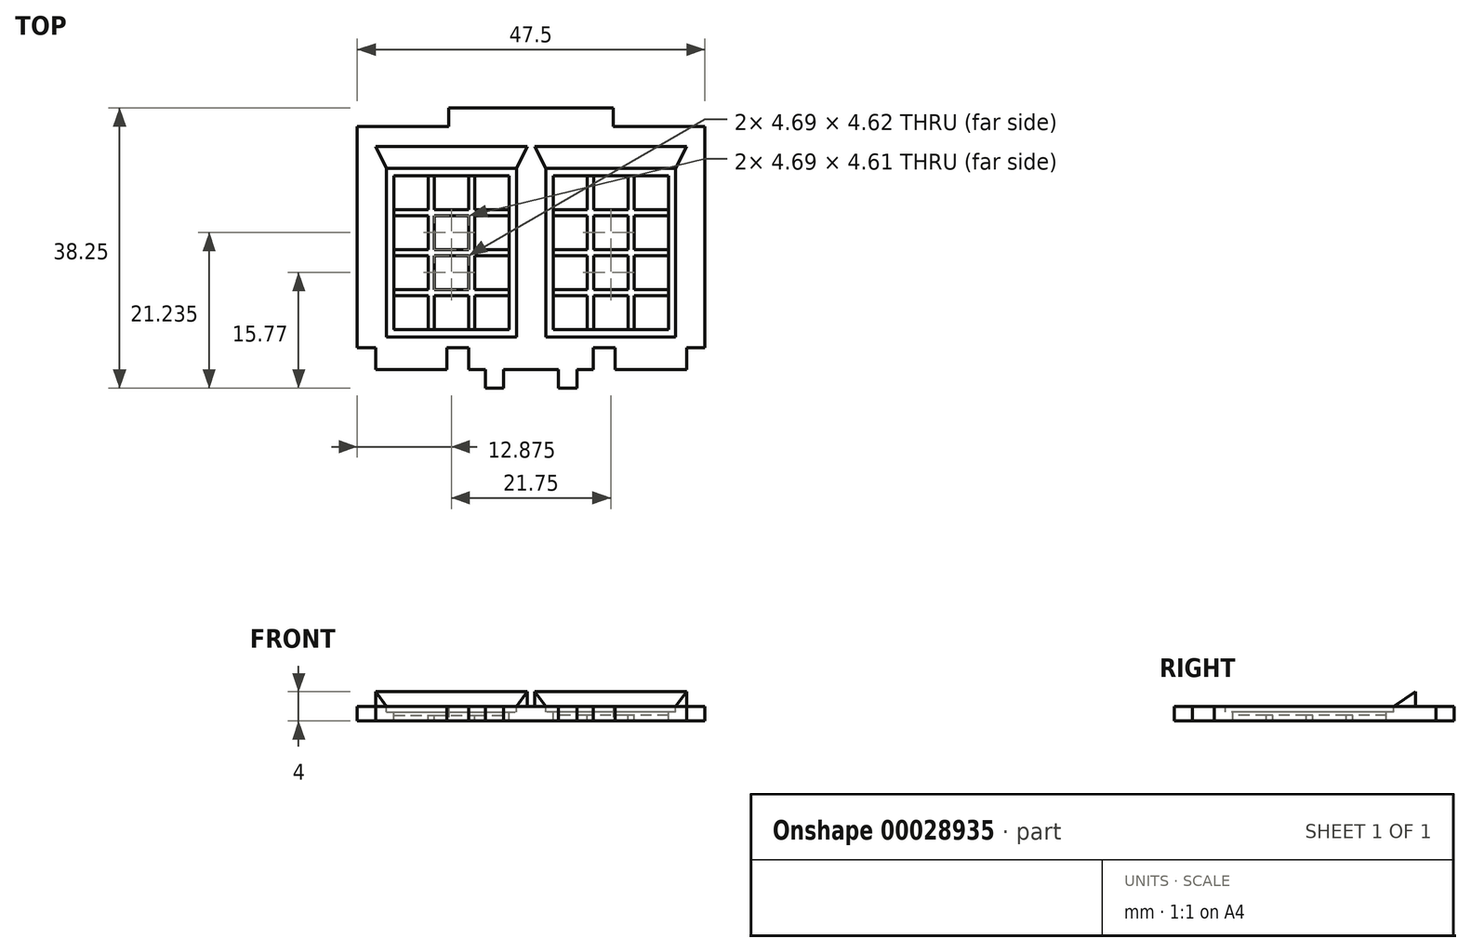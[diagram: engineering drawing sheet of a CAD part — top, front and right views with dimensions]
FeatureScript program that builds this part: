
annotation { "Feature Type Name" : "Feature", "Feature Type Description" : "" }
export const myFeature = defineFeature(function(context is Context, id is Id, definition is map)
    precondition{}
    {
        {
            var Q0;
            Q0=qCreatedBy(makeId("Top.planeOp"),FACE);
            var sketch = newSketch(context, id + "F0", { "sketchPlane" : qUnion([Q0])});
            skLineSegment(sketch, "E0.bottom", {"start": v(-8.5, -5.78) * mm, "end": v(-11.5, -5.78) * mm});
            skLineSegment(sketch, "E0.top", {"start": v(-11.25, 24.47) * mm, "end": v(-23.75, 24.47) * mm});
            skLineSegment(sketch, "E0.right", {"start": v(-23.75, -5.78) * mm, "end": v(-23.75, 24.47) * mm});
            skLineSegment(sketch, "E1.top", {"start": v(-11.25, 26.97) * mm, "end": v(0, 26.97) * mm});
            skLineSegment(sketch, "E1.left", {"start": v(-11.25, 24.47) * mm, "end": v(-11.25, 26.97) * mm});
            skLineSegment(sketch, "E1.right", {"start": v(0, -8.78) * mm, "end": v(0, 26.97) * mm});
            skLineSegment(sketch, "E2.top", {"start": v(-21.25, -8.78) * mm, "end": v(-11.5, -8.78) * mm});
            skLineSegment(sketch, "E2.left", {"start": v(-21.25, -5.78) * mm, "end": v(-21.25, -8.78) * mm});
            skLineSegment(sketch, "E2.right", {"start": v(-11.5, -5.78) * mm, "end": v(-11.5, -8.78) * mm});
            skLineSegment(sketch, "E3.top", {"start": v(-8.5, -8.78) * mm, "end": v(-6.25, -8.78) * mm});
            skLineSegment(sketch, "E3.left", {"start": v(-8.5, -5.78) * mm, "end": v(-8.5, -8.78) * mm});
            skLineSegment(sketch, "E4.top", {"start": v(-6.25, -11.28) * mm, "end": v(-3.75, -11.28) * mm});
            skLineSegment(sketch, "E4.left", {"start": v(-6.25, -8.78) * mm, "end": v(-6.25, -11.28) * mm});
            skLineSegment(sketch, "E4.right", {"start": v(-3.75, -8.78) * mm, "end": v(-3.75, -11.28) * mm});
            skLineSegment(sketch, "E5.trimOffspring", {"start": v(-3.75, -8.78) * mm, "end": v(0, -8.78) * mm});
            skLineSegment(sketch, "E6.trimOffspring", {"start": v(-21.25, -5.78) * mm, "end": v(-23.75, -5.78) * mm});
            skLineSegment(sketch, "E7.MirrorCS", {"start": v(11.25, 26.97) * mm, "end": v(0, 26.97) * mm});
            skLineSegment(sketch, "E8.MirrorCS", {"start": v(11.25, 24.47) * mm, "end": v(11.25, 26.97) * mm});
            skLineSegment(sketch, "E9.MirrorCS", {"start": v(11.25, 24.47) * mm, "end": v(23.75, 24.47) * mm});
            skLineSegment(sketch, "E10.MirrorCS", {"start": v(23.75, -5.78) * mm, "end": v(23.75, 24.47) * mm});
            skLineSegment(sketch, "E11.MirrorCS", {"start": v(21.25, -5.78) * mm, "end": v(23.75, -5.78) * mm});
            skLineSegment(sketch, "E12.MirrorCS", {"start": v(21.25, -5.78) * mm, "end": v(21.25, -8.78) * mm});
            skLineSegment(sketch, "E13.MirrorCS", {"start": v(21.25, -8.78) * mm, "end": v(11.5, -8.78) * mm});
            skLineSegment(sketch, "E14.MirrorCS", {"start": v(11.5, -5.78) * mm, "end": v(11.5, -8.78) * mm});
            skLineSegment(sketch, "E15.MirrorCS", {"start": v(8.5, -5.78) * mm, "end": v(11.5, -5.78) * mm});
            skLineSegment(sketch, "E16.MirrorCS", {"start": v(8.5, -5.78) * mm, "end": v(8.5, -8.78) * mm});
            skLineSegment(sketch, "E17.MirrorCS", {"start": v(8.5, -8.78) * mm, "end": v(6.25, -8.78) * mm});
            skLineSegment(sketch, "E18.MirrorCS", {"start": v(6.25, -8.78) * mm, "end": v(6.25, -11.28) * mm});
            skLineSegment(sketch, "E19.MirrorCS", {"start": v(6.25, -11.28) * mm, "end": v(3.75, -11.28) * mm});
            skLineSegment(sketch, "E20.MirrorCS", {"start": v(3.75, -8.78) * mm, "end": v(3.75, -11.28) * mm});
            skLineSegment(sketch, "E21.MirrorCS", {"start": v(3.75, -8.78) * mm, "end": v(0, -8.78) * mm});
            skSolve(sketch);
        }
        {
            var Q0;
            Q0=makeQuery(id+"F0.imprint","IMPRINT",FACE,{"disambiguationData":[TD([[makeQuery(id+"F0.imprint","IMPRINT",EDGE,{"derivedFrom":sQuery(id+"F0.wireOp",EDGE,"E0.bottom")}),-1.0]])]});
            extrude(context, id + "F1", {"entities" : qUnion([Q0]), "depth" : 2 * mm});
        }
        {
            var Q0;
            Q0=makeQuery(id+"F1.opExtrude","CAP_FACE",FACE,{"disambiguationData":[OSD([sQuery(id+"F0.wireOp",EDGE,"E0.bottom"),sQuery(id+"F0.wireOp",EDGE,"E0.top"),sQuery(id+"F0.wireOp",EDGE,"E0.right"),sQuery(id+"F0.wireOp",EDGE,"E1.top"),sQuery(id+"F0.wireOp",EDGE,"E1.left"),sQuery(id+"F0.wireOp",EDGE,"E1.right"),sQuery(id+"F0.wireOp",EDGE,"E2.top"),sQuery(id+"F0.wireOp",EDGE,"E2.left"),sQuery(id+"F0.wireOp",EDGE,"E2.right"),sQuery(id+"F0.wireOp",EDGE,"E3.top"),sQuery(id+"F0.wireOp",EDGE,"E3.left"),sQuery(id+"F0.wireOp",EDGE,"E4.top"),sQuery(id+"F0.wireOp",EDGE,"E4.left"),sQuery(id+"F0.wireOp",EDGE,"E4.right"),sQuery(id+"F0.wireOp",EDGE,"E5.trimOffspring"),sQuery(id+"F0.wireOp",EDGE,"E6.trimOffspring")])],"isStart":false});
            var sketch = newSketch(context, id + "F2", { "sketchPlane" : qUnion([Q0])});
            skLineSegment(sketch, "E22.bottom", {"start": v(-19.75, 18.72) * mm, "end": v(-2, 18.72) * mm});
            skLineSegment(sketch, "E22.top", {"start": v(-19.75, -4.28) * mm, "end": v(-2, -4.28) * mm});
            skLineSegment(sketch, "E22.left", {"start": v(-19.75, 18.72) * mm, "end": v(-19.75, -4.28) * mm});
            skLineSegment(sketch, "E22.right", {"start": v(-2, 18.72) * mm, "end": v(-2, -4.28) * mm});
            skLineSegment(sketch, "E23", {"start": v(-2, 18.72) * mm, "end": v(-0.5, 21.72) * mm});
            skLineSegment(sketch, "E24", {"start": v(-0.5, 21.72) * mm, "end": v(-21.25, 21.72) * mm});
            skLineSegment(sketch, "E25", {"start": v(-21.25, 21.72) * mm, "end": v(-19.75, 18.72) * mm});
            skLineSegment(sketch, "E26.0", {"start": v(-18.75, 17.72) * mm, "end": v(-3, 17.72) * mm});
            skLineSegment(sketch, "E26.1", {"start": v(-18.75, 17.72) * mm, "end": v(-18.75, -3.28) * mm});
            skLineSegment(sketch, "E26.2", {"start": v(-18.75, -3.28) * mm, "end": v(-3, -3.28) * mm});
            skLineSegment(sketch, "E26.3", {"start": v(-3, 17.72) * mm, "end": v(-3, -3.28) * mm});
            skLineSegment(sketch, "E27", {"start": v(-14.07, 17.72) * mm, "end": v(-14.07, 13.1) * mm});
            skLineSegment(sketch, "E28", {"start": v(-13.22, 17.72) * mm, "end": v(-13.22, 13.1) * mm});
            skLineSegment(sketch, "E29", {"start": v(-8.53, 17.72) * mm, "end": v(-8.53, 13.1) * mm});
            skLineSegment(sketch, "E30", {"start": v(-7.68, 17.72) * mm, "end": v(-7.68, 13.1) * mm});
            skLineSegment(sketch, "E31", {"start": v(-18.75, 13.1) * mm, "end": v(-14.07, 13.1) * mm});
            skLineSegment(sketch, "E32", {"start": v(-18.75, 12.26) * mm, "end": v(-14.07, 12.26) * mm});
            skLineSegment(sketch, "E33", {"start": v(-18.75, 7.65) * mm, "end": v(-14.07, 7.65) * mm});
            skLineSegment(sketch, "E34", {"start": v(-18.75, 6.8) * mm, "end": v(-14.07, 6.8) * mm});
            skLineSegment(sketch, "E35", {"start": v(-18.75, 2.18) * mm, "end": v(-14.07, 2.18) * mm});
            skLineSegment(sketch, "E36", {"start": v(-18.75, 1.33) * mm, "end": v(-14.07, 1.33) * mm});
            skLineSegment(sketch, "E37.trimOffspring", {"start": v(-13.22, 13.1) * mm, "end": v(-8.53, 13.1) * mm});
            skLineSegment(sketch, "E38.trimOffspring", {"start": v(-14.07, 12.26) * mm, "end": v(-14.07, 7.65) * mm});
            skLineSegment(sketch, "E39.trimOffspring", {"start": v(-13.22, 12.26) * mm, "end": v(-8.53, 12.26) * mm});
            skLineSegment(sketch, "E40.trimOffspring", {"start": v(-13.22, 12.26) * mm, "end": v(-13.22, 7.65) * mm});
            skLineSegment(sketch, "E41.trimOffspring", {"start": v(-8.53, 12.26) * mm, "end": v(-8.53, 7.65) * mm});
            skLineSegment(sketch, "E42.trimOffspring", {"start": v(-7.68, 13.1) * mm, "end": v(-3, 13.1) * mm});
            skLineSegment(sketch, "E43.trimOffspring", {"start": v(-7.68, 12.26) * mm, "end": v(-7.68, 7.65) * mm});
            skLineSegment(sketch, "E44.trimOffspring", {"start": v(-7.68, 12.26) * mm, "end": v(-3, 12.26) * mm});
            skLineSegment(sketch, "E45.trimOffspring", {"start": v(-7.68, 7.65) * mm, "end": v(-3, 7.65) * mm});
            skLineSegment(sketch, "E46.trimOffspring", {"start": v(-7.68, 6.8) * mm, "end": v(-7.68, 2.18) * mm});
            skLineSegment(sketch, "E47.trimOffspring", {"start": v(-7.68, 6.8) * mm, "end": v(-3, 6.8) * mm});
            skLineSegment(sketch, "E48.trimOffspring", {"start": v(-8.53, 6.8) * mm, "end": v(-8.53, 2.18) * mm});
            skLineSegment(sketch, "E49.trimOffspring", {"start": v(-13.22, 6.8) * mm, "end": v(-13.22, 2.18) * mm});
            skLineSegment(sketch, "E50.trimOffspring", {"start": v(-13.22, 7.65) * mm, "end": v(-8.53, 7.65) * mm});
            skLineSegment(sketch, "E51.trimOffspring", {"start": v(-14.07, 6.8) * mm, "end": v(-14.07, 2.18) * mm});
            skLineSegment(sketch, "E52.trimOffspring", {"start": v(-13.22, 6.8) * mm, "end": v(-8.53, 6.8) * mm});
            skLineSegment(sketch, "E53.trimOffspring", {"start": v(-13.22, 2.18) * mm, "end": v(-8.53, 2.18) * mm});
            skLineSegment(sketch, "E54.trimOffspring", {"start": v(-14.07, 1.33) * mm, "end": v(-14.07, -3.28) * mm});
            skLineSegment(sketch, "E55.trimOffspring", {"start": v(-13.22, 1.33) * mm, "end": v(-13.22, -3.28) * mm});
            skLineSegment(sketch, "E56.trimOffspring", {"start": v(-13.22, 1.33) * mm, "end": v(-8.53, 1.33) * mm});
            skLineSegment(sketch, "E57.trimOffspring", {"start": v(-7.68, 2.18) * mm, "end": v(-3, 2.18) * mm});
            skLineSegment(sketch, "E58.trimOffspring", {"start": v(-7.68, 1.33) * mm, "end": v(-7.68, -3.28) * mm});
            skLineSegment(sketch, "E59.trimOffspring", {"start": v(-7.68, 1.33) * mm, "end": v(-3, 1.33) * mm});
            skLineSegment(sketch, "E60.trimOffspring", {"start": v(-8.53, 1.33) * mm, "end": v(-8.53, -3.28) * mm});
            skLineSegment(sketch, "E61", {"start": v(-14.07, 17.72) * mm, "end": v(-13.22, 17.72) * mm});
            skLineSegment(sketch, "E62", {"start": v(-18.75, 13.1) * mm, "end": v(-18.75, 12.26) * mm});
            skLineSegment(sketch, "E63", {"start": v(-8.53, 17.72) * mm, "end": v(-7.68, 17.72) * mm});
            skLineSegment(sketch, "E64", {"start": v(-3, 13.1) * mm, "end": v(-3, 12.26) * mm});
            skLineSegment(sketch, "E65", {"start": v(-3, 7.65) * mm, "end": v(-3, 6.8) * mm});
            skLineSegment(sketch, "E66", {"start": v(-18.75, 7.65) * mm, "end": v(-18.75, 6.8) * mm});
            skLineSegment(sketch, "E67", {"start": v(-18.75, 2.18) * mm, "end": v(-18.75, 1.33) * mm});
            skLineSegment(sketch, "E68", {"start": v(-3, 2.18) * mm, "end": v(-3, 1.33) * mm});
            skLineSegment(sketch, "E69", {"start": v(-14.07, -3.28) * mm, "end": v(-13.22, -3.28) * mm});
            skLineSegment(sketch, "E70", {"start": v(-8.53, -3.28) * mm, "end": v(-7.68, -3.28) * mm});
            skLineSegment(sketch, "E71", {"start": v(-14.07, 13.1) * mm, "end": v(-13.22, 13.1) * mm, "construction": true});
            skLineSegment(sketch, "E72", {"start": v(-13.22, 13.1) * mm, "end": v(-13.22, 12.26) * mm, "construction": true});
            skLineSegment(sketch, "E73", {"start": v(-8.53, 7.65) * mm, "end": v(-7.68, 7.65) * mm, "construction": true});
            skLineSegment(sketch, "E74", {"start": v(-7.68, 7.65) * mm, "end": v(-7.68, 6.8) * mm, "construction": true});
            skLineSegment(sketch, "E75", {"start": v(-8.53, 2.18) * mm, "end": v(-8.53, 1.33) * mm, "construction": true});
            skSolve(sketch);
        }
        {
            var Q0;
            Q0=makeQuery(id+"F2.imprint","IMPRINT",FACE,{"disambiguationData":[TD([[makeQuery(id+"F2.imprint","IMPRINT",EDGE,{"derivedFrom":sQuery(id+"F2.wireOp",EDGE,"E26.0")}),-1.0]])]});
            var Q1;
            {var subQ1=sQuery(id+"F2.wireOp",EDGE,"E32");Q1=makeQuery(id+"F2.imprint","IMPRINT",FACE,{"disambiguationData":[TD([[makeQuery(id+"F2.imprint","IMPRINT",EDGE,{"derivedFrom":subQ1}),-1.0]])]});}
            var Q2;
            Q2=makeQuery(id+"F2.imprint","IMPRINT",FACE,{"disambiguationData":[TD([[makeQuery(id+"F2.imprint","IMPRINT",EDGE,{"derivedFrom":sQuery(id+"F2.wireOp",EDGE,"E39.trimOffspring")}),-1.0]])]});
            var Q3;
            Q3=makeQuery(id+"F2.imprint","IMPRINT",FACE,{"disambiguationData":[TD([[makeQuery(id+"F2.imprint","IMPRINT",EDGE,{"derivedFrom":sQuery(id+"F2.wireOp",EDGE,"E43.trimOffspring")}),1.0]])]});
            var Q4;
            Q4=makeQuery(id+"F2.imprint","IMPRINT",FACE,{"disambiguationData":[TD([[makeQuery(id+"F2.imprint","IMPRINT",EDGE,{"derivedFrom":sQuery(id+"F2.wireOp",EDGE,"E46.trimOffspring")}),1.0]])]});
            var Q5;
            Q5=makeQuery(id+"F2.imprint","IMPRINT",FACE,{"disambiguationData":[TD([[makeQuery(id+"F2.imprint","IMPRINT",EDGE,{"derivedFrom":sQuery(id+"F2.wireOp",EDGE,"E48.trimOffspring")}),-1.0]])]});
            var Q6;
            {var subQ1=sQuery(id+"F2.wireOp",EDGE,"E34");Q6=makeQuery(id+"F2.imprint","IMPRINT",FACE,{"disambiguationData":[TD([[makeQuery(id+"F2.imprint","IMPRINT",EDGE,{"derivedFrom":subQ1}),-1.0]])]});}
            var Q7;
            {var subQ1=sQuery(id+"F2.wireOp",EDGE,"E36");Q7=makeQuery(id+"F2.imprint","IMPRINT",FACE,{"disambiguationData":[TD([[makeQuery(id+"F2.imprint","IMPRINT",EDGE,{"derivedFrom":subQ1}),-1.0]])]});}
            var Q8;
            {var subQ1=sQuery(id+"F2.wireOp",EDGE,"E55.trimOffspring");Q8=makeQuery(id+"F2.imprint","IMPRINT",FACE,{"disambiguationData":[TD([[makeQuery(id+"F2.imprint","IMPRINT",EDGE,{"derivedFrom":subQ1}),1.0]])]});}
            var Q9;
            {var subQ1=sQuery(id+"F2.wireOp",EDGE,"E58.trimOffspring");Q9=makeQuery(id+"F2.imprint","IMPRINT",FACE,{"disambiguationData":[TD([[makeQuery(id+"F2.imprint","IMPRINT",EDGE,{"derivedFrom":subQ1}),1.0]])]});}
            extrude(context, id + "F3", {"entities" : qUnion([Q0, Q1, Q2, Q3, Q4, Q5, Q6, Q7, Q8, Q9]), "operationType" : NewBodyOperationType.REMOVE, "endBound" : BoundingType.THROUGH_ALL, "oppositeDirection" : true, "depth" : 25 * mm});
        }
        {
            var Q0;
            Q0=makeQuery(id+"F2.imprint","IMPRINT",FACE,{"disambiguationData":[TD([[makeQuery(id+"F2.imprint","IMPRINT",EDGE,{"derivedFrom":sQuery(id+"F2.wireOp",EDGE,"E22.top")}),1.0]])]});
            extrude(context, id + "F4", {"entities" : qUnion([Q0]), "operationType" : NewBodyOperationType.REMOVE, "oppositeDirection" : true, "depth" : (2 - 1.2) * mm});
        }
        {
            var Q0;
            Q0=makeQuery(id+"F2.imprint","IMPRINT",FACE,{"disambiguationData":[TD([[makeQuery(id+"F2.imprint","IMPRINT",EDGE,{"derivedFrom":sQuery(id+"F2.wireOp",EDGE,"E22.bottom")}),1.0]])]});
            extrude(context, id + "F5", {"entities" : qUnion([Q0]), "operationType" : NewBodyOperationType.ADD, "depth" : 2 * mm});
        }
        {
            var Q0;
            Q0=makeQuery(id+"F1.opExtrude","SWEPT_FACE",FACE,{"disambiguationData":[OSD([sQuery(id+"F0.wireOp",EDGE,"E1.left")])]});
            var sketch = newSketch(context, id + "F6", { "sketchPlane" : qUnion([Q0])});
            skLineSegment(sketch, "E76.0", {"start": v(-18.72, 2) * mm, "end": v(-21.72, 2) * mm});
            skLineSegment(sketch, "E77.0", {"start": v(-21.72, 4) * mm, "end": v(-18.72, 4) * mm});
            skLineSegment(sketch, "E78", {"start": v(-18.72, 2) * mm, "end": v(-21.72, 4) * mm});
            skLineSegment(sketch, "E79", {"start": v(-18.72, 4) * mm, "end": v(-18.72, 2) * mm});
            skSolve(sketch);
        }
        {
            var Q0;
            Q0 = qSketchRegion(id + "F6", true);
            extrude(context, id + "F7", {"entities" : qUnion([Q0]), "operationType" : NewBodyOperationType.REMOVE, "endBound" : BoundingType.SYMMETRIC, "oppositeDirection" : true, "depth" : 500 * mm});
        }
        {
            var Q0;
            Q0=makeQuery(id+"F2.imprint","IMPRINT",FACE,{"disambiguationData":[TD([[makeQuery(id+"F2.imprint","IMPRINT",EDGE,{"derivedFrom":sQuery(id+"F2.wireOp",EDGE,"E27")}),1.0]])]});
            extrude(context, id + "F8", {"entities" : qUnion([Q0]), "operationType" : NewBodyOperationType.REMOVE, "oppositeDirection" : true, "depth" : (2 - 0.8) * mm});
        }
        {
            var Q0;
            Q0=makeQuery(id+"F1.opExtrude","SWEPT_BODY",BODY,{"disambiguationData":[OSD([sQuery(id+"F0.wireOp",EDGE,"E0.bottom"),sQuery(id+"F0.wireOp",EDGE,"E0.top"),sQuery(id+"F0.wireOp",EDGE,"E0.right"),sQuery(id+"F0.wireOp",EDGE,"E1.top"),sQuery(id+"F0.wireOp",EDGE,"E1.left"),sQuery(id+"F0.wireOp",EDGE,"E1.right"),sQuery(id+"F0.wireOp",EDGE,"E2.top"),sQuery(id+"F0.wireOp",EDGE,"E2.left"),sQuery(id+"F0.wireOp",EDGE,"E2.right"),sQuery(id+"F0.wireOp",EDGE,"E3.top"),sQuery(id+"F0.wireOp",EDGE,"E3.left"),sQuery(id+"F0.wireOp",EDGE,"E4.top"),sQuery(id+"F0.wireOp",EDGE,"E4.left"),sQuery(id+"F0.wireOp",EDGE,"E4.right"),sQuery(id+"F0.wireOp",EDGE,"E5.trimOffspring"),sQuery(id+"F0.wireOp",EDGE,"E6.trimOffspring")])]});
            var Q1;
            Q1=qCreatedBy(makeId("Right.planeOp"),FACE);
            mirror(context, id + "F9", {"operationType" : NewBodyOperationType.ADD, "entities" : qUnion([Q0]), "mirrorPlane" : qUnion([Q1])});
        }
    });
